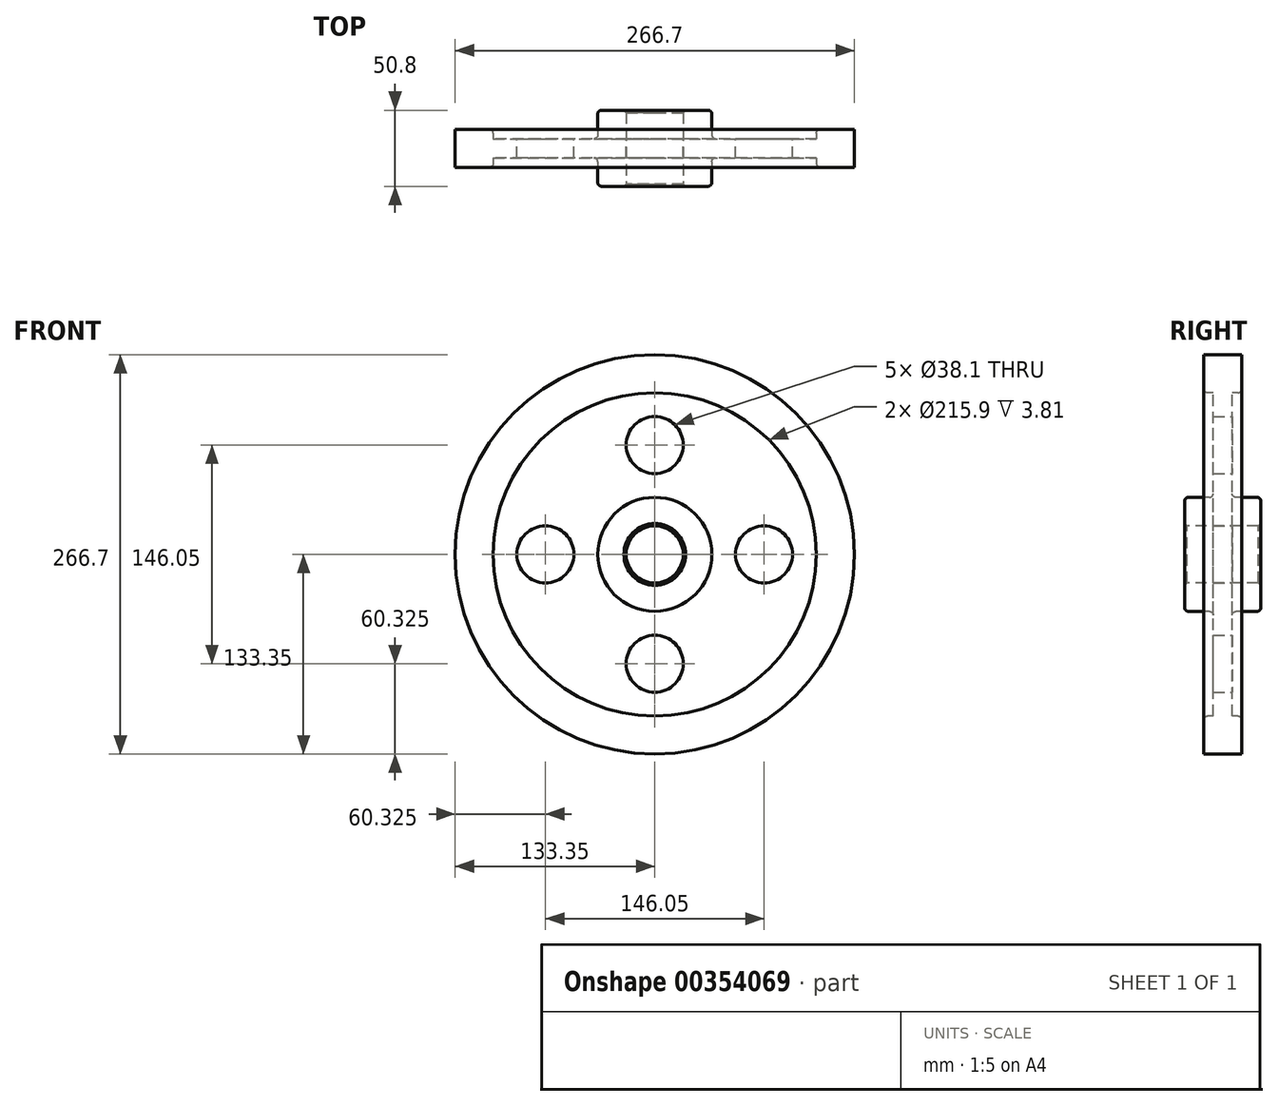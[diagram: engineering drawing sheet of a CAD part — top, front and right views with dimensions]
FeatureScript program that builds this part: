
annotation { "Feature Type Name" : "Feature", "Feature Type Description" : "" }
export const myFeature = defineFeature(function(context is Context, id is Id, definition is map)
    precondition{}
    {
        {
            var Q0;
            Q0=qCreatedBy(makeId("Right.planeOp"),FACE);
            var sketch = newSketch(context, id + "F0", { "sketchPlane" : qUnion([Q0])});
            skLineSegment(sketch, "E0", {"start": v(0, 0) * mm, "end": v(75.6, 0) * mm, "construction": true});
            skLineSegment(sketch, "E1.0", {"start": v(6.35, 38.1) * mm, "end": v(25.4, 38.1) * mm});
            skLineSegment(sketch, "E2.0", {"start": v(6.35, 107.95) * mm, "end": v(12.7, 107.95) * mm});
            skLineSegment(sketch, "E3.0", {"start": v(0, 133.35) * mm, "end": v(12.7, 133.35) * mm});
            skLineSegment(sketch, "E4.0", {"start": v(0, 19.05) * mm, "end": v(25.4, 19.05) * mm});
            skLineSegment(sketch, "E5", {"start": v(0, 0) * mm, "end": v(0, 133.35) * mm, "construction": true});
            skLineSegment(sketch, "E6.0", {"start": v(25.4, 19.05) * mm, "end": v(25.4, 38.1) * mm});
            skLineSegment(sketch, "E7.0", {"start": v(6.35, 38.1) * mm, "end": v(6.35, 107.95) * mm});
            skLineSegment(sketch, "E8.0", {"start": v(12.7, 107.95) * mm, "end": v(12.7, 133.35) * mm});
            skLineSegment(sketch, "E9.MirrorCS", {"start": v(-25.4, 19.05) * mm, "end": v(-25.4, 38.1) * mm});
            skLineSegment(sketch, "E10.MirrorCS", {"start": v(-6.35, 38.1) * mm, "end": v(-25.4, 38.1) * mm});
            skLineSegment(sketch, "E11.MirrorCS", {"start": v(-6.35, 38.1) * mm, "end": v(-6.35, 107.95) * mm});
            skLineSegment(sketch, "E12.MirrorCS", {"start": v(0, 19.05) * mm, "end": v(-25.4, 19.05) * mm});
            skLineSegment(sketch, "E13.MirrorCS", {"start": v(-12.7, 107.95) * mm, "end": v(-12.7, 133.35) * mm});
            skLineSegment(sketch, "E14.MirrorCS", {"start": v(0, 133.35) * mm, "end": v(-12.7, 133.35) * mm});
            skLineSegment(sketch, "E15", {"start": v(-12.7, 107.95) * mm, "end": v(-6.35, 107.95) * mm});
            skSolve(sketch);
        }
        {
            var Q0;
            Q0=makeQuery(id+"F0.imprint","IMPRINT",FACE,{"disambiguationData":[TD([[makeQuery(id+"F0.imprint","IMPRINT",EDGE,{"derivedFrom":sQuery(id+"F0.wireOp",EDGE,"E1.0")}),-1.0]])]});
            var Q1;
            Q1=sQuery(id+"F0.wireOp",EDGE,"E0");
            revolve(context, id + "F1", {"entities" : qUnion([Q0]), "axis" : qUnion([Q1]), "revolveType" : RevolveType.FULL});
        }
        {
            var Q0;
            Q0=makeQuery(id+"F1.opRevolve","SWEPT_FACE",FACE,{"disambiguationData":[OSD([sQuery(id+"F0.wireOp",EDGE,"E7.0")])]});
            var sketch = newSketch(context, id + "F2", { "sketchPlane" : qUnion([Q0])});
            skLineSegment(sketch, "E16", {"start": v(0, 0) * mm, "end": v(0, 73.03) * mm});
            skCircle(sketch, "E17", {"center": v(0, 73.03) * mm, "radius": 19.05 * mm});
            skCircle(sketch, "E18.1.0", {"center": v(-73.03, 0) * mm, "radius": 19.05 * mm});
            skCircle(sketch, "E18.2.0", {"center": v(0, -73.03) * mm, "radius": 19.05 * mm});
            skCircle(sketch, "E18.3.0", {"center": v(73.03, 0) * mm, "radius": 19.05 * mm});
            skPoint(sketch, "E18.center", {"position": v(0, 0) * mm});
            skSolve(sketch);
        }
        {
            var Q0;
            Q0=makeQuery(id+"F2.imprint","IMPRINT",FACE,{"disambiguationData":[TD([[makeQuery(id+"F2.imprint","IMPRINT",EDGE,{"derivedFrom":sQuery(id+"F2.wireOp",EDGE,"E18.1.0")}),1.0]])]});
            var Q1;
            Q1=makeQuery(id+"F2.imprint","IMPRINT",FACE,{"disambiguationData":[TD([[makeQuery(id+"F2.imprint","IMPRINT",EDGE,{"derivedFrom":sQuery(id+"F2.wireOp",EDGE,"E18.2.0")}),1.0]])]});
            var Q2;
            Q2=makeQuery(id+"F2.imprint","IMPRINT",FACE,{"disambiguationData":[TD([[makeQuery(id+"F2.imprint","IMPRINT",EDGE,{"derivedFrom":sQuery(id+"F2.wireOp",EDGE,"E18.3.0")}),1.0]])]});
            var Q3;
            Q3=makeQuery(id+"F2.imprint","IMPRINT",FACE,{"disambiguationData":[TD([[makeQuery(id+"F2.imprint","IMPRINT",EDGE,{"derivedFrom":sQuery(id+"F2.wireOp",EDGE,"E17")}),1.0]])]});
            extrude(context, id + "F3", {"entities" : qUnion([Q0, Q1, Q2, Q3]), "operationType" : NewBodyOperationType.REMOVE, "oppositeDirection" : true, "depth" : 25.4 * mm});
        }
        {
            var Q0;
            Q0=makeQuery(id+"F1.opRevolve","SWEPT_EDGE",EDGE,{"disambiguationData":[OSD([sQuery(id+"F0.wireOp",EDGE,"E1.0"),sQuery(id+"F0.wireOp",EDGE,"E7.0")])]});
            var Q1;
            Q1=makeQuery(id+"F1.opRevolve","SWEPT_EDGE",EDGE,{"disambiguationData":[OSD([sQuery(id+"F0.wireOp",EDGE,"E1.0"),sQuery(id+"F0.wireOp",EDGE,"E6.0")])]});
            var Q2;
            Q2=makeQuery(id+"F1.opRevolve","SWEPT_EDGE",EDGE,{"disambiguationData":[OSD([sQuery(id+"F0.wireOp",EDGE,"E8.0"),sQuery(id+"F0.wireOp",EDGE,"E2.0")])]});
            var Q3;
            Q3=makeQuery(id+"F1.opRevolve","SWEPT_EDGE",EDGE,{"disambiguationData":[OSD([sQuery(id+"F0.wireOp",EDGE,"E9.MirrorCS"),sQuery(id+"F0.wireOp",EDGE,"E10.MirrorCS")])]});
            var Q4;
            Q4=makeQuery(id+"F1.opRevolve","SWEPT_EDGE",EDGE,{"disambiguationData":[OSD([sQuery(id+"F0.wireOp",EDGE,"E11.MirrorCS"),sQuery(id+"F0.wireOp",EDGE,"E10.MirrorCS")])]});
            var Q5;
            Q5=makeQuery(id+"F1.opRevolve","SWEPT_EDGE",EDGE,{"disambiguationData":[OSD([sQuery(id+"F0.wireOp",EDGE,"E13.MirrorCS"),sQuery(id+"F0.wireOp",EDGE,"E15")])]});
            fillet(context, id + "F4", {"entities" : qUnion([Q0, Q1, Q2, Q3, Q4, Q5]), "radius" : 2.54 * mm, "tangentPropagation" : true, "allowEdgeOverflow" : false});
        }
        {
            var Q0;
            Q0=makeQuery(id+"F1.opRevolve","SWEPT_EDGE",EDGE,{"disambiguationData":[OSD([sQuery(id+"F0.wireOp",EDGE,"E9.MirrorCS"),sQuery(id+"F0.wireOp",EDGE,"E12.MirrorCS")])]});
            var Q1;
            Q1=makeQuery(id+"F1.opRevolve","SWEPT_EDGE",EDGE,{"disambiguationData":[OSD([sQuery(id+"F0.wireOp",EDGE,"E6.0"),sQuery(id+"F0.wireOp",EDGE,"E4.0")])]});
            chamfer(context, id + "F5", {"entities" : qUnion([Q0, Q1]), "width" : 1.59 * mm, "tangentPropagation" : true});
        }
    });
